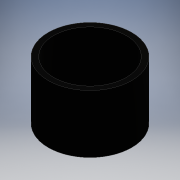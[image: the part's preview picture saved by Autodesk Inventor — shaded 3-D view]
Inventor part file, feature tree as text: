
AUTODESK INVENTOR PART (.ipt)
format: ipt  version: 2016 (Build 200138000, 138)  size: 91,136 bytes
history: native  units: mm
features: other x1, sketch x1, extrude x1
ambient origin geometry x8: Origin, YZ Plane, XZ Plane, XY Plane, X Axis, Y Axis, Z Axis, Center Point
bodies: Body1 (feature_tree)
feature tree (3):
  other  "ソリッド1"
  sketch  "スケッチ1"
  extrude  "押し出し1"  Depth=20.0mm
